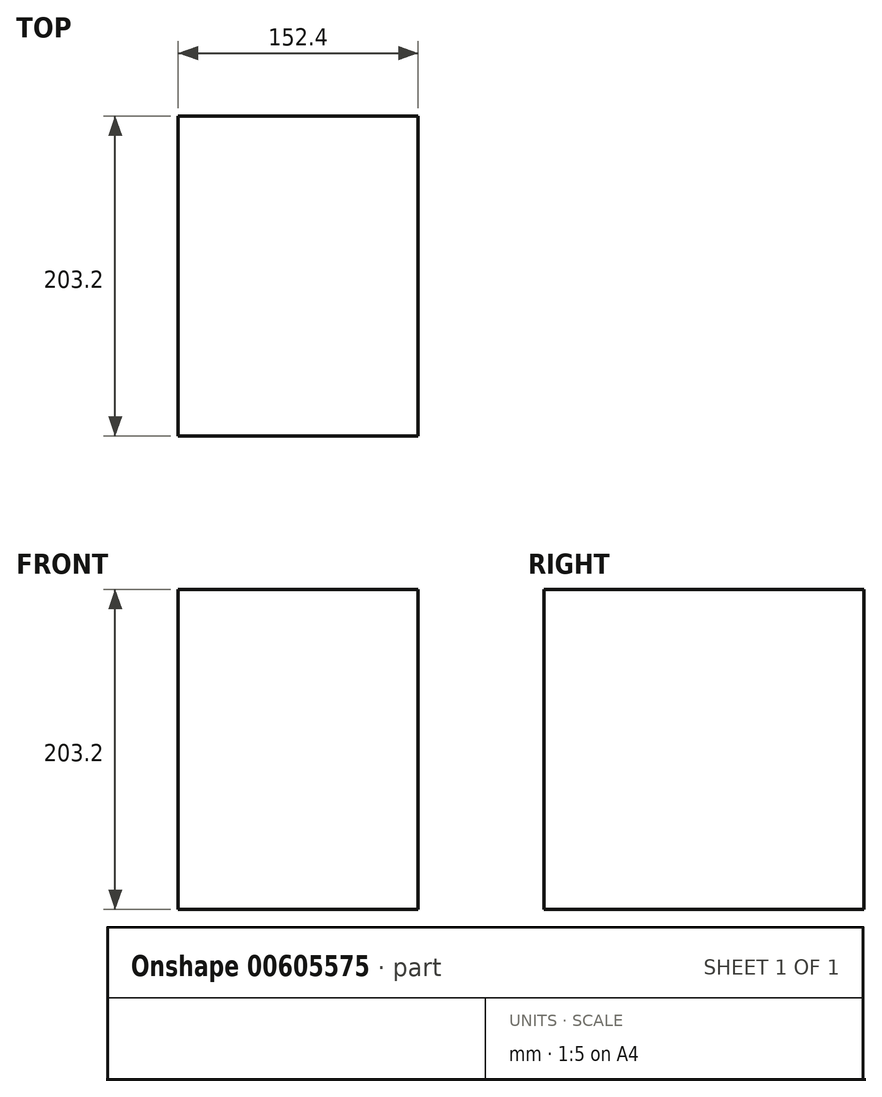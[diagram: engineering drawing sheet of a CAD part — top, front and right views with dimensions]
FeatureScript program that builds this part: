
annotation { "Feature Type Name" : "Feature", "Feature Type Description" : "" }
export const myFeature = defineFeature(function(context is Context, id is Id, definition is map)
    precondition{}
    {
        {
            var Q0;
            Q0=qCreatedBy(makeId("Front.planeOp"),FACE);
            var sketch = newSketch(context, id + "F0", { "sketchPlane" : qUnion([Q0])});
            skLineSegment(sketch, "E0.bottom", {"start": v(-75.14, 142.08) * mm, "end": v(77.26, 142.08) * mm});
            skLineSegment(sketch, "E0.top", {"start": v(-75.14, -61.12) * mm, "end": v(77.26, -61.12) * mm});
            skLineSegment(sketch, "E0.left", {"start": v(-75.14, 142.08) * mm, "end": v(-75.14, -61.12) * mm});
            skLineSegment(sketch, "E0.right", {"start": v(77.26, 142.08) * mm, "end": v(77.26, -61.12) * mm});
            skSolve(sketch);
        }
        {
            var Q0;
            Q0=makeQuery(id+"F0.imprint","IMPRINT",FACE,{"disambiguationData":[TD([[makeQuery(id+"F0.imprint","IMPRINT",EDGE,{"derivedFrom":sQuery(id+"F0.wireOp",EDGE,"E0.bottom")}),-1.0]])]});
            extrude(context, id + "F1", {"entities" : qUnion([Q0]), "depth" : 203.2 * mm, "offsetDistance" : 25.4 * mm});
        }
    });
